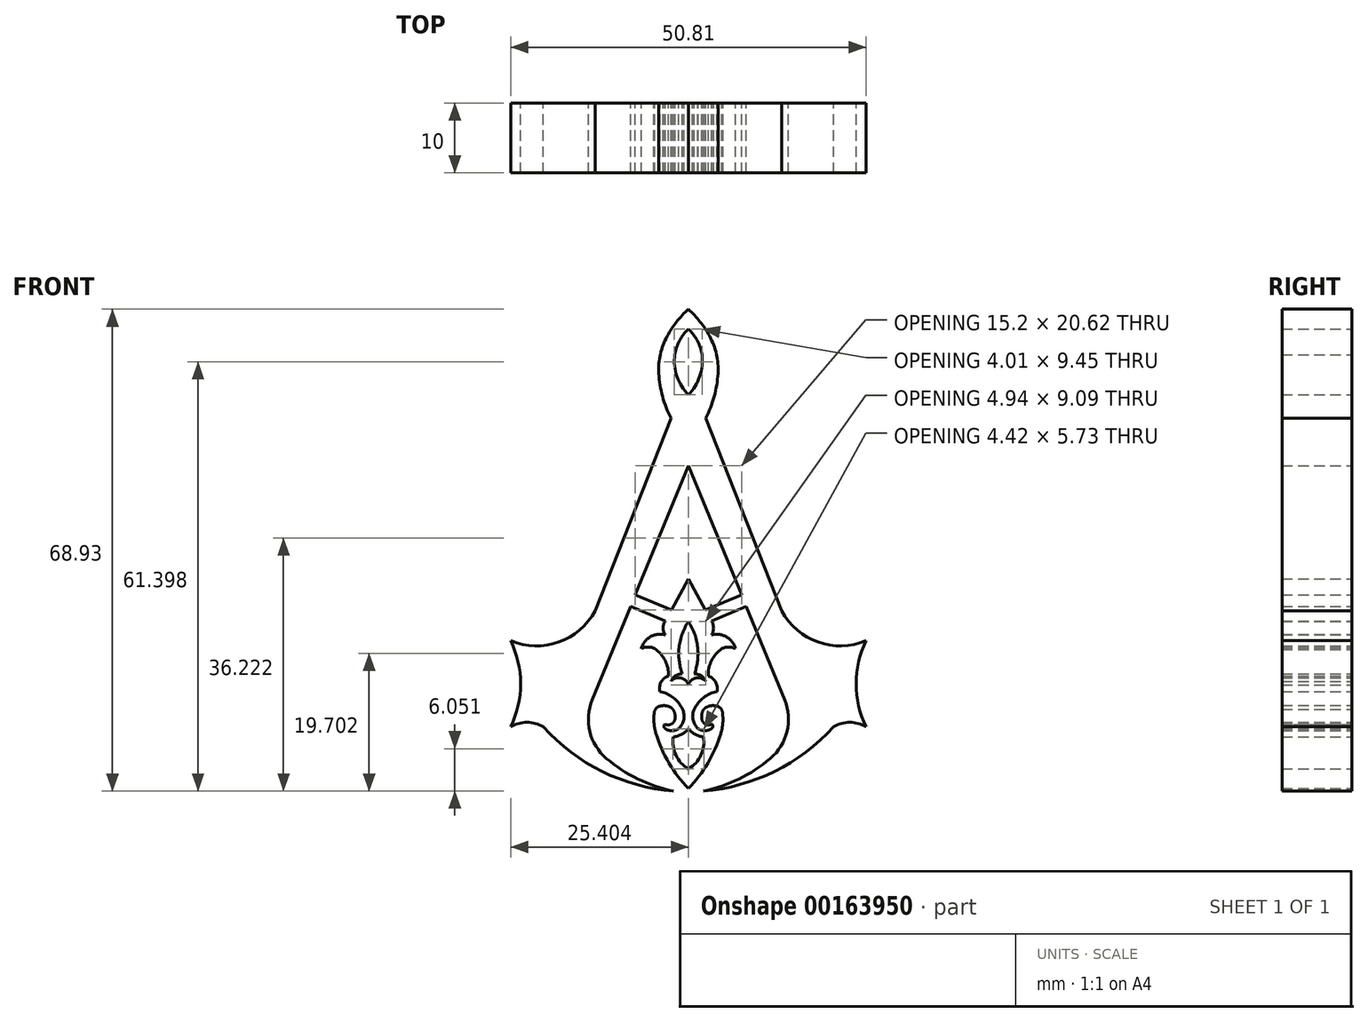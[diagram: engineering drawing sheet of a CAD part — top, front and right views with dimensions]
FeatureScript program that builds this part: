
annotation { "Feature Type Name" : "Feature", "Feature Type Description" : "" }
export const myFeature = defineFeature(function(context is Context, id is Id, definition is map)
    precondition{}
    {
        {
            var Q0;
            Q0=qCreatedBy(makeId("Front.planeOp"),FACE);
            var sketch = newSketch(context, id + "F0", { "sketchPlane" : qUnion([Q0])});
            skArc(sketch, "E0", {"start": v(-32.75, 97.62) * mm, "mid": v(-35.27, 94.64) * mm, "end": v(-36.9, 91.1) * mm});
            skArc(sketch, "E1", {"start": v(-36.9, 91.1) * mm, "mid": v(-36.74, 86.45) * mm, "end": v(-35.23, 82.05) * mm});
            skArc(sketch, "E2", {"start": v(-32.75, 94.81) * mm, "mid": v(-34.02, 93.12) * mm, "end": v(-34.7, 91.1) * mm});
            skArc(sketch, "E3", {"start": v(-34.7, 91.1) * mm, "mid": v(-34.37, 88.01) * mm, "end": v(-32.75, 85.36) * mm});
            skLineSegment(sketch, "E4", {"start": v(-35.23, 82.05) * mm, "end": v(-46.07, 54.5) * mm});
            skArc(sketch, "E5", {"start": v(-58.15, 50.2) * mm, "mid": v(-51.28, 50) * mm, "end": v(-46.07, 54.5) * mm});
            skArc(sketch, "E6", {"start": v(-58.15, 37.87) * mm, "mid": v(-56.74, 44.03) * mm, "end": v(-58.15, 50.2) * mm});
            skArc(sketch, "E7", {"start": v(-53.5, 37.87) * mm, "mid": v(-55.82, 38.52) * mm, "end": v(-58.15, 37.87) * mm});
            skArc(sketch, "E8", {"start": v(-46.07, 34.85) * mm, "mid": v(-40.96, 30.92) * mm, "end": v(-34.9, 28.69) * mm});
            skArc(sketch, "E9", {"start": v(-53.5, 37.87) * mm, "mid": v(-45.08, 31.5) * mm, "end": v(-34.9, 28.69) * mm});
            skArc(sketch, "E10", {"start": v(-46.68, 41.3) * mm, "mid": v(-47.1, 38) * mm, "end": v(-46.07, 34.85) * mm});
            skLineSegment(sketch, "E11", {"start": v(-46.68, 41.3) * mm, "end": v(-32.75, 75.22) * mm});
            skArc(sketch, "E12", {"start": v(-37.54, 37.47) * mm, "mid": v(-35.67, 32.96) * mm, "end": v(-32.75, 29.04) * mm});
            skArc(sketch, "E13", {"start": v(-37.54, 40.4) * mm, "mid": v(-37.69, 38.93) * mm, "end": v(-37.54, 37.47) * mm});
            skArc(sketch, "E14", {"start": v(-34.97, 40.4) * mm, "mid": v(-36.25, 40.92) * mm, "end": v(-37.54, 40.4) * mm});
            skArc(sketch, "E15", {"start": v(-34.97, 38.27) * mm, "mid": v(-34.63, 39.33) * mm, "end": v(-34.97, 40.4) * mm});
            skArc(sketch, "E16", {"start": v(-36.12, 38.27) * mm, "mid": v(-35.54, 38.12) * mm, "end": v(-34.97, 38.27) * mm});
            skArc(sketch, "E17", {"start": v(-36.12, 38.27) * mm, "mid": v(-36.24, 37.96) * mm, "end": v(-36.12, 37.66) * mm});
            skArc(sketch, "E18", {"start": v(-36.12, 37.66) * mm, "mid": v(-35.11, 37.33) * mm, "end": v(-34.1, 37.66) * mm});
            skArc(sketch, "E19", {"start": v(-34.1, 37.66) * mm, "mid": v(-33.4, 38.94) * mm, "end": v(-33.6, 40.4) * mm});
            skArc(sketch, "E20", {"start": v(-33.6, 40.4) * mm, "mid": v(-34.9, 42.05) * mm, "end": v(-36.83, 42.92) * mm});
            skArc(sketch, "E21", {"start": v(-35.59, 45.16) * mm, "mid": v(-36.64, 44.29) * mm, "end": v(-36.83, 42.92) * mm});
            skArc(sketch, "E22", {"start": v(-35.59, 45.16) * mm, "mid": v(-36.07, 47.36) * mm, "end": v(-37.54, 49.05) * mm});
            skArc(sketch, "E23", {"start": v(-37.54, 49.05) * mm, "mid": v(-38.52, 49.29) * mm, "end": v(-39.49, 49.05) * mm});
            skArc(sketch, "E24", {"start": v(-36.04, 51.02) * mm, "mid": v(-38.17, 50.75) * mm, "end": v(-39.49, 49.05) * mm});
            skArc(sketch, "E25", {"start": v(-36.04, 53.03) * mm, "mid": v(-36.35, 52.02) * mm, "end": v(-36.04, 51.02) * mm});
            skLineSegment(sketch, "E26", {"start": v(-36.04, 53.03) * mm, "end": v(-32.75, 59.07) * mm});
            skArc(sketch, "E27", {"start": v(-32.75, 52.94) * mm, "mid": v(-33.68, 51.01) * mm, "end": v(-34.1, 48.92) * mm});
            skArc(sketch, "E28", {"start": v(-34.1, 48.92) * mm, "mid": v(-34.04, 47.15) * mm, "end": v(-33.6, 45.43) * mm});
            skArc(sketch, "E29", {"start": v(-33.6, 45.43) * mm, "mid": v(-34.58, 45.18) * mm, "end": v(-35.21, 44.4) * mm});
            skArc(sketch, "E30", {"start": v(-34.89, 36.43) * mm, "mid": v(-33.7, 36.8) * mm, "end": v(-32.75, 37.6) * mm});
            skArc(sketch, "E31", {"start": v(-34.89, 36.43) * mm, "mid": v(-34.54, 33.81) * mm, "end": v(-32.75, 31.88) * mm});
            skArc(sketch, "E32.MirrorCS", {"start": v(-29.38, 38.27) * mm, "mid": v(-29.95, 38.12) * mm, "end": v(-30.53, 38.27) * mm});
            skArc(sketch, "E33.MirrorCS", {"start": v(-27.95, 40.4) * mm, "mid": v(-27.8, 38.93) * mm, "end": v(-27.95, 37.47) * mm});
            skArc(sketch, "E34.MirrorCS", {"start": v(-30.53, 38.27) * mm, "mid": v(-30.86, 39.33) * mm, "end": v(-30.53, 40.4) * mm});
            skArc(sketch, "E35.MirrorCS", {"start": v(-29.38, 38.27) * mm, "mid": v(-29.25, 37.96) * mm, "end": v(-29.38, 37.66) * mm});
            skArc(sketch, "E36.MirrorCS", {"start": v(-29.38, 37.66) * mm, "mid": v(-30.38, 37.33) * mm, "end": v(-31.38, 37.66) * mm});
            skArc(sketch, "E37.MirrorCS", {"start": v(-30.53, 40.4) * mm, "mid": v(-29.24, 40.92) * mm, "end": v(-27.95, 40.4) * mm});
            skArc(sketch, "E38.MirrorCS", {"start": v(-31.89, 45.43) * mm, "mid": v(-30.91, 45.18) * mm, "end": v(-30.28, 44.4) * mm});
            skArc(sketch, "E39.MirrorCS", {"start": v(-31.9, 40.4) * mm, "mid": v(-30.58, 42.05) * mm, "end": v(-28.67, 42.92) * mm});
            skArc(sketch, "E40.MirrorCS", {"start": v(-30.6, 36.43) * mm, "mid": v(-31.8, 36.8) * mm, "end": v(-32.75, 37.6) * mm});
            skArc(sketch, "E41.MirrorCS", {"start": v(-31.38, 37.66) * mm, "mid": v(-32.1, 38.94) * mm, "end": v(-31.9, 40.4) * mm});
            skArc(sketch, "E42.MirrorCS", {"start": v(-29.9, 45.16) * mm, "mid": v(-28.85, 44.29) * mm, "end": v(-28.67, 42.92) * mm});
            skArc(sketch, "E43.MirrorCS", {"start": v(-32.75, 52.94) * mm, "mid": v(-31.82, 51.01) * mm, "end": v(-31.38, 48.92) * mm});
            skArc(sketch, "E44.MirrorCS", {"start": v(-29.46, 51.02) * mm, "mid": v(-27.32, 50.75) * mm, "end": v(-26, 49.05) * mm});
            skArc(sketch, "E45.MirrorCS", {"start": v(-29.9, 45.16) * mm, "mid": v(-29.42, 47.36) * mm, "end": v(-27.95, 49.05) * mm});
            skArc(sketch, "E46.MirrorCS", {"start": v(-12, 37.87) * mm, "mid": v(-9.67, 38.52) * mm, "end": v(-7.34, 37.87) * mm});
            skArc(sketch, "E47.MirrorCS", {"start": v(-31.38, 48.92) * mm, "mid": v(-31.46, 47.15) * mm, "end": v(-31.89, 45.43) * mm});
            skArc(sketch, "E48.MirrorCS", {"start": v(-29.46, 53.03) * mm, "mid": v(-29.15, 52.02) * mm, "end": v(-29.46, 51.02) * mm});
            skArc(sketch, "E49.MirrorCS", {"start": v(-27.95, 49.05) * mm, "mid": v(-26.98, 49.29) * mm, "end": v(-26, 49.05) * mm});
            skLineSegment(sketch, "E50.MirrorCS", {"start": v(-29.46, 53.03) * mm, "end": v(-32.75, 59.07) * mm});
            skArc(sketch, "E51.MirrorCS", {"start": v(-30.6, 36.43) * mm, "mid": v(-30.95, 33.81) * mm, "end": v(-32.75, 31.88) * mm});
            skArc(sketch, "E52.MirrorCS", {"start": v(-30.8, 91.1) * mm, "mid": v(-31.12, 88.01) * mm, "end": v(-32.75, 85.36) * mm});
            skArc(sketch, "E53.MirrorCS", {"start": v(-32.75, 94.81) * mm, "mid": v(-31.47, 93.12) * mm, "end": v(-30.8, 91.1) * mm});
            skLineSegment(sketch, "E54.MirrorCS", {"start": v(-18.81, 41.3) * mm, "end": v(-32.75, 75.22) * mm});
            skArc(sketch, "E55.MirrorCS", {"start": v(-7.34, 37.87) * mm, "mid": v(-8.75, 44.03) * mm, "end": v(-7.34, 50.2) * mm});
            skArc(sketch, "E56.MirrorCS", {"start": v(-7.34, 50.2) * mm, "mid": v(-14.22, 50) * mm, "end": v(-19.42, 54.5) * mm});
            skLineSegment(sketch, "E57.MirrorCS", {"start": v(-30.26, 82.05) * mm, "end": v(-19.42, 54.5) * mm});
            skArc(sketch, "E58.MirrorCS", {"start": v(-28.59, 91.1) * mm, "mid": v(-28.75, 86.45) * mm, "end": v(-30.26, 82.05) * mm});
            skArc(sketch, "E59.MirrorCS", {"start": v(-18.81, 41.3) * mm, "mid": v(-18.38, 38) * mm, "end": v(-19.42, 34.85) * mm});
            skArc(sketch, "E60.MirrorCS", {"start": v(-12, 37.87) * mm, "mid": v(-20.41, 31.5) * mm, "end": v(-30.59, 28.69) * mm});
            skArc(sketch, "E61.MirrorCS", {"start": v(-19.42, 34.85) * mm, "mid": v(-24.53, 30.92) * mm, "end": v(-30.59, 28.69) * mm});
            skArc(sketch, "E62.MirrorCS", {"start": v(-27.95, 37.47) * mm, "mid": v(-29.82, 32.96) * mm, "end": v(-32.75, 29.04) * mm});
            skArc(sketch, "E63.MirrorCS", {"start": v(-32.75, 97.62) * mm, "mid": v(-30.23, 94.64) * mm, "end": v(-28.59, 91.1) * mm});
            skArc(sketch, "E64", {"start": v(-32.75, 43.85) * mm, "mid": v(-33.81, 44.86) * mm, "end": v(-35.21, 44.4) * mm});
            skArc(sketch, "E65.MirrorCS", {"start": v(-32.75, 43.85) * mm, "mid": v(-31.68, 44.86) * mm, "end": v(-30.28, 44.4) * mm});
            skLineSegment(sketch, "E66", {"start": v(-36.04, 53.03) * mm, "end": v(-41.02, 55.07) * mm});
            skLineSegment(sketch, "E67", {"start": v(-40.35, 56.72) * mm, "end": v(-35.18, 54.6) * mm});
            skLineSegment(sketch, "E68", {"start": v(-32.75, 52.94) * mm, "end": v(-32.75, 46.18) * mm});
            skLineSegment(sketch, "E69.MirrorCS", {"start": v(-25.15, 56.72) * mm, "end": v(-30.31, 54.6) * mm});
            skLineSegment(sketch, "E70.MirrorCS", {"start": v(-29.46, 53.03) * mm, "end": v(-24.47, 55.07) * mm});
            skSolve(sketch);
        }
        {
            var Q0;
            Q0=makeQuery(id+"F0.imprint","IMPRINT",FACE,{"disambiguationData":[TD([[makeQuery(id+"F0.imprint","IMPRINT",EDGE,{"derivedFrom":sQuery(id+"F0.wireOp",EDGE,"E0")}),1.0]])]});
            var Q1;
            Q1=makeQuery(id+"F0.imprint","IMPRINT",FACE,{"disambiguationData":[TD([[makeQuery(id+"F0.imprint","IMPRINT",EDGE,{"derivedFrom":sQuery(id+"F0.wireOp",EDGE,"E12")}),1.0]])]});
            var Q2;
            {var subQ0=sQuery(id+"F0.wireOp",EDGE,"E66");Q2=makeQuery(id+"F0.imprint","IMPRINT",FACE,{"disambiguationData":[TD([[makeQuery(id+"F0.imprint","IMPRINT",EDGE,{"derivedFrom":subQ0}),-1.0]])]});}
            var Q3;
            {var subQ2=sQuery(id+"F0.wireOp",EDGE,"E69.MirrorCS");Q3=makeQuery(id+"F0.imprint","IMPRINT",FACE,{"disambiguationData":[TD([[makeQuery(id+"F0.imprint","IMPRINT",EDGE,{"derivedFrom":subQ2}),1.0]])]});}
            extrude(context, id + "F1", {"entities" : qUnion([Q0, Q1, Q2, Q3]), "depth" : 5 * mm, "hasSecondDirection" : true, "secondDirectionOppositeDirection" : true, "secondDirectionDepth" : 5 * mm});
        }
        {
            var Q0;
            Q0=makeQuery(id+"F1.opExtrude","SWEPT_EDGE",EDGE,{"disambiguationData":[OSD([sQuery(id+"F0.wireOp",EDGE,"E13"),sQuery(id+"F0.wireOp",EDGE,"E14")])]});
            var Q1;
            Q1=makeQuery(id+"F1.opExtrude","SWEPT_EDGE",EDGE,{"disambiguationData":[OSD([sQuery(id+"F0.wireOp",EDGE,"E14"),sQuery(id+"F0.wireOp",EDGE,"E15")])]});
            var Q2;
            Q2=makeQuery(id+"F1.opExtrude","SWEPT_EDGE",EDGE,{"disambiguationData":[OSD([sQuery(id+"F0.wireOp",EDGE,"E15"),sQuery(id+"F0.wireOp",EDGE,"E16")])]});
            var Q3;
            Q3=makeQuery(id+"F1.opExtrude","SWEPT_EDGE",EDGE,{"disambiguationData":[OSD([sQuery(id+"F0.wireOp",EDGE,"E33.MirrorCS"),sQuery(id+"F0.wireOp",EDGE,"E37.MirrorCS")])]});
            var Q4;
            Q4=makeQuery(id+"F1.opExtrude","SWEPT_EDGE",EDGE,{"disambiguationData":[OSD([sQuery(id+"F0.wireOp",EDGE,"E34.MirrorCS"),sQuery(id+"F0.wireOp",EDGE,"E37.MirrorCS")])]});
            var Q5;
            Q5=makeQuery(id+"F1.opExtrude","SWEPT_EDGE",EDGE,{"disambiguationData":[OSD([sQuery(id+"F0.wireOp",EDGE,"E32.MirrorCS"),sQuery(id+"F0.wireOp",EDGE,"E34.MirrorCS")])]});
            fillet(context, id + "F2", {"entities" : qUnion([Q0, Q1, Q2, Q3, Q4, Q5]), "radius" : 1 * mm, "tangentPropagation" : true, "allowEdgeOverflow" : false});
        }
        {
            var Q0;
            Q0=makeQuery(id+"F1.opExtrude","SWEPT_EDGE",EDGE,{"disambiguationData":[OSD([sQuery(id+"F0.wireOp",EDGE,"E12"),sQuery(id+"F0.wireOp",EDGE,"E13")])]});
            var Q1;
            Q1=makeQuery(id+"F1.opExtrude","SWEPT_EDGE",EDGE,{"disambiguationData":[OSD([sQuery(id+"F0.wireOp",EDGE,"E33.MirrorCS"),sQuery(id+"F0.wireOp",EDGE,"E62.MirrorCS")])]});
            fillet(context, id + "F3", {"entities" : qUnion([Q0, Q1]), "radius" : 7 * mm, "tangentPropagation" : true, "allowEdgeOverflow" : false});
        }
        {
            var Q0;
            Q0=makeQuery(id+"F1.opExtrude","SWEPT_EDGE",EDGE,{"disambiguationData":[OSD([sQuery(id+"F0.wireOp",EDGE,"E0"),sQuery(id+"F0.wireOp",EDGE,"E1")])]});
            var Q1;
            Q1=makeQuery(id+"F1.opExtrude","SWEPT_EDGE",EDGE,{"disambiguationData":[OSD([sQuery(id+"F0.wireOp",EDGE,"E58.MirrorCS"),sQuery(id+"F0.wireOp",EDGE,"E63.MirrorCS")])]});
            fillet(context, id + "F4", {"entities" : qUnion([Q0, Q1]), "radius" : 10 * mm, "tangentPropagation" : true, "allowEdgeOverflow" : false});
        }
        {
            var Q0;
            Q0=makeQuery(id+"F1.opExtrude","SWEPT_EDGE",EDGE,{"disambiguationData":[OSD([sQuery(id+"F0.wireOp",EDGE,"E8"),sQuery(id+"F0.wireOp",EDGE,"E10")])]});
            var Q1;
            Q1=makeQuery(id+"F1.opExtrude","SWEPT_EDGE",EDGE,{"disambiguationData":[OSD([sQuery(id+"F0.wireOp",EDGE,"E59.MirrorCS"),sQuery(id+"F0.wireOp",EDGE,"E61.MirrorCS")])]});
            fillet(context, id + "F5", {"entities" : qUnion([Q0, Q1]), "radius" : 7.34 * mm, "tangentPropagation" : true, "allowEdgeOverflow" : false});
        }
    });
